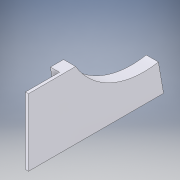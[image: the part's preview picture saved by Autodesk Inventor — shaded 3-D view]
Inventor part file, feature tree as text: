
AUTODESK INVENTOR PART (.ipt)
format: ipt  version: 2019 (Build 230136000, 136)  size: 124,928 bytes
history: native  units: in
note: dims shown in document units (in); Inventor stores cm internally (conversion verified against a paired STEP export)
features: extrude x2, sketch x2, fillet x1
ambient origin geometry x8: Origin, YZ Plane, XZ Plane, XY Plane, X Axis, Y Axis, Z Axis, Center Point
bodies: Solid1 (feature_tree)
feature tree (5):
  extrude  "Extrusion1"  Depth=1.1818in
  fillet  "Fillet2"  Radius=0.8858in
  extrude  "Extrusion3"  Depth=0.0787in
  sketch  "Sketch1"  dims[d14=0.1181in d15=0.0in d27=1.1818in d28=0.8858in]
  sketch  "Sketch3"  dims[d29=0.6788in d31=0.0787in d32=0.4429in d33=0.0394in d34=0.0in d35=0.3877in d36=0.5497in d37=1.0271in d38=0.5212in]
